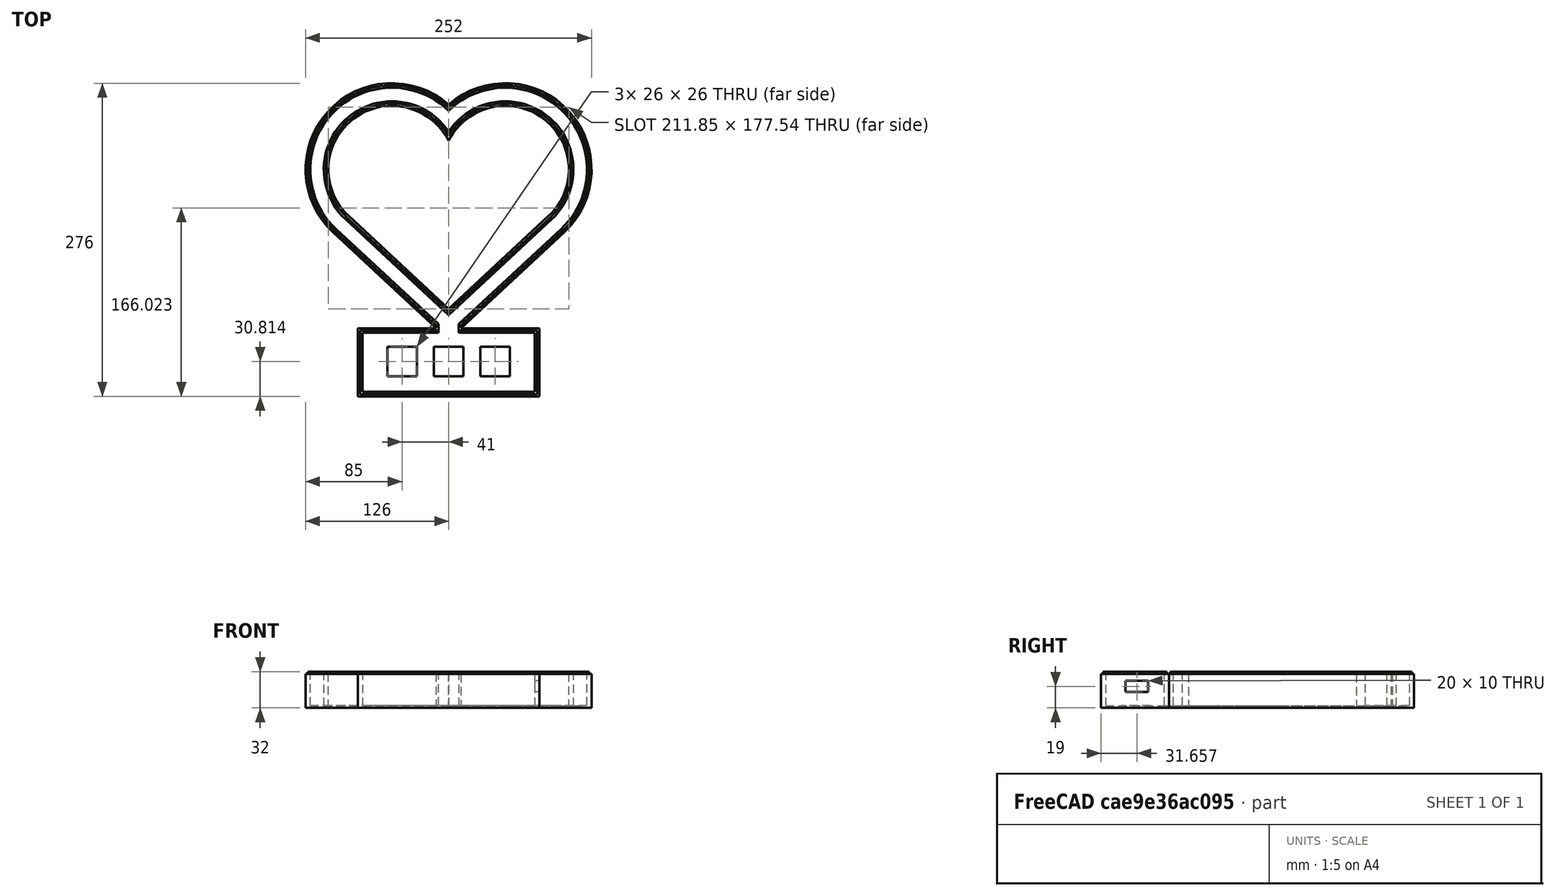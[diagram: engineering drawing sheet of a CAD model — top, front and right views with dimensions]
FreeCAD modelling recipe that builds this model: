
FCSTD DOCUMENT  (FreeCAD 0.19R24291 (Git))
Label: heart_tube_bottom_thick
License: All rights reserved
LicenseURL: http://en.wikipedia.org/wiki/All_rights_reserved
objects: TechDraw::DrawViewDimension×15, Sketcher::SketchObject×12, PartDesign::Pocket×7, PartDesign::Pad×5, TechDraw::DrawViewPart×2, PartDesign::Body×1, TechDraw::DrawSVGTemplate×1, TechDraw::DrawViewDetail×1, TechDraw::DrawPage×1
note: 37 computed .brp shape members not serialized (recipe doc carries the construction recipe); baked Part::Feature solids carry a one-line shape summary decoded from their .brp

FEATURE [Sketcher::SketchObject] Sketch
  AttachmentOffset = pos=(0,0,32) rot=(0,0,1;0rad)
  FullyConstrained = true
  MapMode = 5
  Placement = pos=(0,0,32) rot=(0,0,1;0rad)
  Support = -> [XY_Plane]
  sketch-geometry (4):
    g0: ArcOfCircle CenterX=-50 CenterY=0 CenterZ=0 NormalX=0 NormalY=0 NormalZ=1 AngleXU=0 Radius=56 StartAngle=0.467146 EndAngle=3.96463
    g1: ArcOfCircle CenterX=50 CenterY=0 CenterZ=0 NormalX=0 NormalY=0 NormalZ=1 AngleXU=0 Radius=56 StartAngle=5.46015 EndAngle=8.95763
    g2: LineSegment StartX=-88.08 StartY=-41.0599 StartZ=0 EndX=0 EndY=-122.748 EndZ=0
    g3: LineSegment StartX=0 StartY=-122.748 StartZ=0 EndX=88.08 EndY=-41.0599 EndZ=0
  constraints (11):
    c: Symmetric(g0,g1,g-2)
    c: Equal(g1,g0)
    c: Coincident(g0,g1)
    c: PointOnObject(g2,g-2)
    c: Coincident(g3,g2)
    c: Tangent(g3,g1) = -1.5708
    c: Tangent(g2,g0) = -1.5708
    c: DistanceX(g0,g1) = 100
    c: PointOnObject(g1,g-1)
    c: Distance(g-1,g2) = 90
    c: Radius(g1) = 56
FEATURE [Sketcher::SketchObject] Sketch001
  FullyConstrained = true
  MapMode = 5
  Support = -> [XY_Plane]
  sketch-geometry (4):
    g0: ArcOfCircle CenterX=-50 CenterY=0 CenterZ=0 NormalX=0 NormalY=0 NormalZ=1 AngleXU=0 Radius=76 StartAngle=0.852776 EndAngle=3.96463
    g1: ArcOfCircle CenterX=50 CenterY=0 CenterZ=0 NormalX=0 NormalY=0 NormalZ=1 AngleXU=0 Radius=76 StartAngle=5.46015 EndAngle=8.572
    g2: LineSegment StartX=-101.68 StartY=-55.7241 StartZ=0 EndX=0 EndY=-150.025 EndZ=0
    g3: LineSegment StartX=0 StartY=-150.025 StartZ=0 EndX=101.68 EndY=-55.7241 EndZ=0
  constraints (11):
    c: Symmetric(g0,g1,g-2)
    c: Equal(g1,g0)
    c: Coincident(g0,g1)
    c: PointOnObject(g2,g-2)
    c: Coincident(g3,g2)
    c: Tangent(g3,g1) = -1.5708
    c: Tangent(g2,g0) = -1.5708
    c: DistanceX(g0,g1) = 100
    c: PointOnObject(g1,g-1)
    c: Distance(g-1,g2) = 110
    c: Radius(g1) = 76
FEATURE [Sketcher::SketchObject] Sketch002
  FullyConstrained = true
  MapMode = 5
  Support = -> [XY_Plane]
  sketch-geometry (4):
    g0: ArcOfCircle CenterX=-50 CenterY=0 CenterZ=0 NormalX=0 NormalY=0 NormalZ=1 AngleXU=0 Radius=74 StartAngle=0.828915 EndAngle=3.96463
    g1: ArcOfCircle CenterX=50 CenterY=0 CenterZ=0 NormalX=0 NormalY=0 NormalZ=1 AngleXU=0 Radius=74 StartAngle=5.46015 EndAngle=8.59586
    g2: LineSegment StartX=-100.32 StartY=-54.2577 StartZ=0 EndX=0 EndY=-147.297 EndZ=0
    g3: LineSegment StartX=0 StartY=-147.297 StartZ=0 EndX=100.32 EndY=-54.2577 EndZ=0
  constraints (11):
    c: Symmetric(g0,g1,g-2)
    c: Equal(g1,g0)
    c: Coincident(g0,g1)
    c: PointOnObject(g2,g-2)
    c: Coincident(g3,g2)
    c: Tangent(g3,g1) = -1.5708
    c: Tangent(g2,g0) = -1.5708
    c: DistanceX(g0,g1) = 100
    c: PointOnObject(g1,g-1)
    c: Distance(g-1,g2) = 108
    c: Radius(g1) = 74
FEATURE [Sketcher::SketchObject] Sketch003
  AttachmentOffset = pos=(0,0,32) rot=(0,0,1;0rad)
  FullyConstrained = true
  MapMode = 5
  Placement = pos=(0,0,32) rot=(0,0,1;0rad)
  Support = -> [XY_Plane]
  sketch-geometry (4):
    g0: ArcOfCircle CenterX=-50 CenterY=0 CenterZ=0 NormalX=0 NormalY=0 NormalZ=1 AngleXU=0 Radius=58 StartAngle=0.531458 EndAngle=3.96463
    g1: ArcOfCircle CenterX=50 CenterY=0 CenterZ=0 NormalX=0 NormalY=0 NormalZ=1 AngleXU=0 Radius=58 StartAngle=5.46015 EndAngle=8.89332
    g2: LineSegment StartX=-89.44 StartY=-42.5263 StartZ=0 EndX=0 EndY=-125.475 EndZ=0
    g3: LineSegment StartX=0 StartY=-125.475 StartZ=0 EndX=89.44 EndY=-42.5263 EndZ=0
  constraints (11):
    c: Symmetric(g0,g1,g-2)
    c: Equal(g1,g0)
    c: Coincident(g0,g1)
    c: PointOnObject(g2,g-2)
    c: Coincident(g3,g2)
    c: Tangent(g3,g1) = -1.5708
    c: Tangent(g2,g0) = -1.5708
    c: DistanceX(g0,g1) = 100
    c: PointOnObject(g1,g-1)
    c: Distance(g-1,g2) = 92
    c: Radius(g1) = 58
FEATURE [PartDesign::Pad] Pad
  Direction = (1,1,1)
  Length = 30
  Length2 = 100
  Profile = -> Sketch001
  Refine = true
  Type = 0
FEATURE [Sketcher::SketchObject] Sketch004
  FullyConstrained = true
  MapMode = 5
  Support = -> [XY_Plane]
  sketch-geometry (4):
    g0: LineSegment StartX=-80 StartY=-140 StartZ=0 EndX=80 EndY=-140 EndZ=0
    g1: LineSegment StartX=80 StartY=-140 StartZ=0 EndX=80 EndY=-200 EndZ=0
    g2: LineSegment StartX=80 StartY=-200 StartZ=0 EndX=-80 EndY=-200 EndZ=0
    g3: LineSegment StartX=-80 StartY=-200 StartZ=0 EndX=-80 EndY=-140 EndZ=0
  constraints (11):
    c: Coincident(g0,g1)
    c: Coincident(g1,g2)
    c: Coincident(g2,g3)
    c: Coincident(g3,g0)
    c: Horizontal(g2)
    c: Vertical(g1)
    c: Vertical(g3)
    c: DistanceY(g1,g1) = 60
    c: DistanceX(g0,g0) = 160
    c: Symmetric(g0,g0,g-2)
    c: DistanceY(g0,g-1) = 140
FEATURE [Sketcher::SketchObject] Sketch005
  FullyConstrained = true
  MapMode = 5
  Support = -> [XY_Plane]
  sketch-geometry (4):
    g0: LineSegment StartX=-78 StartY=-142 StartZ=0 EndX=78 EndY=-142 EndZ=0
    g1: LineSegment StartX=78 StartY=-142 StartZ=0 EndX=78 EndY=-198 EndZ=0
    g2: LineSegment StartX=78 StartY=-198 StartZ=0 EndX=-78 EndY=-198 EndZ=0
    g3: LineSegment StartX=-78 StartY=-198 StartZ=0 EndX=-78 EndY=-142 EndZ=0
  constraints (11):
    c: Coincident(g0,g1)
    c: Coincident(g1,g2)
    c: Coincident(g2,g3)
    c: Coincident(g3,g0)
    c: Horizontal(g2)
    c: Vertical(g1)
    c: Vertical(g3)
    c: DistanceY(g1,g1) = 56
    c: DistanceX(g0,g0) = 156
    c: Symmetric(g0,g0,g-2)
    c: DistanceY(g0,g-1) = 142
FEATURE [Sketcher::SketchObject] Sketch006
  AttachmentOffset = pos=(0,0,32) rot=(0,0,1;0rad)
  FullyConstrained = false
  MapMode = 5
  Placement = pos=(0,0,32) rot=(0,0,1;0rad)
  Support = -> [XY_Plane]
  sketch-geometry (4):
    g0: LineSegment StartX=-9 StartY=-136.077 StartZ=0 EndX=9 EndY=-136.077 EndZ=0
    g1: LineSegment StartX=9 StartY=-136.077 StartZ=0 EndX=9 EndY=-148.077 EndZ=0
    g2: LineSegment StartX=9 StartY=-148.077 StartZ=0 EndX=-9 EndY=-148.077 EndZ=0
    g3: LineSegment StartX=-9 StartY=-148.077 StartZ=0 EndX=-9 EndY=-136.077 EndZ=0
  constraints (10):
    c: Coincident(g0,g1)
    c: Coincident(g1,g2)
    c: Coincident(g2,g3)
    c: Coincident(g3,g0)
    c: Horizontal(g0)
    c: Vertical(g1)
    c: Vertical(g3)
    c: DistanceY(g1,g1) = 12
    c: DistanceX(g0,g0) = 18
    c: Symmetric(g1,g2,g-2)
FEATURE [PartDesign::Pad] Pad003
  BaseFeature = -> Pad
  Direction = (1,1,1)
  Length = 32
  Length2 = 100
  Profile = -> Sketch002
  Refine = true
  Type = 0
FEATURE [Sketcher::SketchObject] Sketch007
  AttachmentOffset = pos=(0,0,32) rot=(0,0,1;0rad)
  FullyConstrained = true
  MapMode = 5
  Placement = pos=(0,0,32) rot=(0,0,1;0rad)
  Support = -> [XY_Plane]
  sketch-geometry (4):
    g0: ArcOfCircle CenterX=-50 CenterY=0 CenterZ=0 NormalX=0 NormalY=0 NormalZ=1 AngleXU=0 Radius=72 StartAngle=0.803149 EndAngle=3.96463
    g1: ArcOfCircle CenterX=50 CenterY=0 CenterZ=0 NormalX=0 NormalY=0 NormalZ=1 AngleXU=0 Radius=72 StartAngle=5.46015 EndAngle=8.62163
    g2: LineSegment StartX=-98.96 StartY=-52.7913 StartZ=0 EndX=-1.42e-14 EndY=-144.569 EndZ=0
    g3: LineSegment StartX=-1.42e-14 StartY=-144.569 StartZ=0 EndX=98.96 EndY=-52.7913 EndZ=0
  constraints (11):
    c: Symmetric(g0,g1,g-2)
    c: Equal(g1,g0)
    c: Coincident(g0,g1)
    c: PointOnObject(g2,g-2)
    c: Coincident(g3,g2)
    c: Tangent(g3,g1) = -1.5708
    c: Tangent(g2,g0) = -1.5708
    c: DistanceX(g0,g1) = 100
    c: PointOnObject(g1,g-1)
    c: Distance(g-1,g2) = 106
    c: Radius(g1) = 72
FEATURE [PartDesign::Pocket] Pocket
  BaseFeature = -> Pad003
  Length = 30
  Length2 = 100
  Profile = -> Sketch007
  Refine = true
  Type = 0
FEATURE [Sketcher::SketchObject] Sketch008
  FullyConstrained = true
  MapMode = 5
  Support = -> [XY_Plane]
  sketch-geometry (4):
    g0: ArcOfCircle CenterX=-50 CenterY=0 CenterZ=0 NormalX=0 NormalY=0 NormalZ=1 AngleXU=0 Radius=60 StartAngle=0.585686 EndAngle=3.96463
    g1: ArcOfCircle CenterX=50 CenterY=0 CenterZ=0 NormalX=0 NormalY=0 NormalZ=1 AngleXU=0 Radius=60 StartAngle=5.46015 EndAngle=8.83909
    g2: LineSegment StartX=-90.8 StartY=-43.9927 StartZ=0 EndX=0 EndY=-128.203 EndZ=0
    g3: LineSegment StartX=0 StartY=-128.203 StartZ=0 EndX=90.8 EndY=-43.9927 EndZ=0
  constraints (11):
    c: Symmetric(g0,g1,g-2)
    c: Equal(g1,g0)
    c: Coincident(g0,g1)
    c: PointOnObject(g2,g-2)
    c: Coincident(g3,g2)
    c: Tangent(g3,g1) = -1.5708
    c: Tangent(g2,g0) = -1.5708
    c: DistanceX(g0,g1) = 100
    c: PointOnObject(g1,g-1)
    c: Distance(g-1,g2) = 94
    c: Radius(g1) = 60
FEATURE [PartDesign::Pad] Pad004
  BaseFeature = -> Pocket
  Direction = (1,1,1)
  Length = 32
  Length2 = 100
  Profile = -> Sketch008
  Refine = true
  Type = 0
FEATURE [PartDesign::Pocket] Pocket004
  BaseFeature = -> Pad004
  Length = 2
  Length2 = 100
  Profile = -> Sketch003
  Refine = true
  Type = 0
FEATURE [PartDesign::Pocket] Pocket001
  BaseFeature = -> Pocket004
  Length = 25
  Length2 = 100
  Profile = -> Sketch
  Refine = true
  Type = 1
FEATURE [PartDesign::Pad] Pad002
  BaseFeature = -> Pocket001
  Direction = (1,1,1)
  Length = 30
  Length2 = 100
  Profile = -> Sketch004
  Refine = true
  Type = 0
FEATURE [Sketcher::SketchObject] Sketch009
  AttachmentOffset = pos=(0,0,32) rot=(0,0,1;0rad)
  FullyConstrained = true
  MapMode = 5
  Placement = pos=(0,0,32) rot=(0,0,1;0rad)
  Support = -> [XY_Plane]
  sketch-geometry (4):
    g0: LineSegment StartX=-76 StartY=-144 StartZ=0 EndX=76 EndY=-144 EndZ=0
    g1: LineSegment StartX=76 StartY=-144 StartZ=0 EndX=76 EndY=-196 EndZ=0
    g2: LineSegment StartX=76 StartY=-196 StartZ=0 EndX=-76 EndY=-196 EndZ=0
    g3: LineSegment StartX=-76 StartY=-196 StartZ=0 EndX=-76 EndY=-144 EndZ=0
  constraints (11):
    c: Coincident(g0,g1)
    c: Coincident(g1,g2)
    c: Coincident(g2,g3)
    c: Coincident(g3,g0)
    c: Horizontal(g2)
    c: Vertical(g1)
    c: Vertical(g3)
    c: DistanceY(g1,g1) = 52
    c: DistanceX(g0,g0) = 152
    c: Symmetric(g0,g0,g-2)
    c: DistanceY(g0,g-1) = 144
FEATURE [PartDesign::Pad] Pad005
  BaseFeature = -> Pad002
  Direction = (1,1,1)
  Length = 32
  Length2 = 100
  Profile = -> Sketch005
  Refine = true
  Type = 0
FEATURE [PartDesign::Pocket] Pocket006
  BaseFeature = -> Pad005
  Length = 30
  Length2 = 100
  Profile = -> Sketch009
  Refine = true
  Type = 0
FEATURE [PartDesign::Pocket] Pocket005
  BaseFeature = -> Pocket006
  Length = 30
  Length2 = 100
  Profile = -> Sketch006
  Refine = true
  Type = 0
FEATURE [Sketcher::SketchObject] Sketch010
  AttachmentOffset = pos=(0,0,80) rot=(0,0,1;0rad)
  ExternalGeometry = -> [Pocket005]
  FullyConstrained = false
  MapMode = 5
  Placement = pos=(80,-1.78e-14,1.78e-14) rot=(0.57735,0.57735,0.57735;2.0944rad)
  Support = -> [YZ_Plane]
  sketch-geometry (4):
    g0: LineSegment StartX=-178.343 StartY=24 StartZ=0 EndX=-158.343 EndY=24 EndZ=0
    g1: LineSegment StartX=-158.343 StartY=24 StartZ=0 EndX=-158.343 EndY=14 EndZ=0
    g2: LineSegment StartX=-158.343 StartY=14 StartZ=0 EndX=-178.343 EndY=14 EndZ=0
    g3: LineSegment StartX=-178.343 StartY=14 StartZ=0 EndX=-178.343 EndY=24 EndZ=0
  constraints (11):
    c: Coincident(g0,g1)
    c: Coincident(g1,g2)
    c: Coincident(g2,g3)
    c: Coincident(g3,g0)
    c: Horizontal(g0)
    c: Horizontal(g2)
    c: Vertical(g1)
    c: Vertical(g3)
    c: DistanceX(g0,g0) = 20
    c: DistanceY(g1,g1) = 10
    c: DistanceY(g-3,g1) = 12
FEATURE [PartDesign::Pocket] Pocket007
  BaseFeature = -> Pocket005
  Length = 10
  Length2 = 100
  Midplane = true
  Profile = -> Sketch010
  Refine = true
  Type = 0
FEATURE [Sketcher::SketchObject] Sketch011
  FullyConstrained = false
  MapMode = 5
  Support = -> [XY_Plane]
  sketch-geometry (12):
    g0: LineSegment StartX=-54 StartY=-156.186 StartZ=0 EndX=-28 EndY=-156.186 EndZ=0
    g1: LineSegment StartX=-28 StartY=-156.186 StartZ=0 EndX=-28 EndY=-182.186 EndZ=0
    g2: LineSegment StartX=-28 StartY=-182.186 StartZ=0 EndX=-54 EndY=-182.186 EndZ=0
    g3: LineSegment StartX=-54 StartY=-182.186 StartZ=0 EndX=-54 EndY=-156.186 EndZ=0
    g4: LineSegment StartX=-13 StartY=-156.186 StartZ=0 EndX=13 EndY=-156.186 EndZ=0
    g5: LineSegment StartX=13 StartY=-156.186 StartZ=0 EndX=13 EndY=-182.186 EndZ=0
    g6: LineSegment StartX=13 StartY=-182.186 StartZ=0 EndX=-13 EndY=-182.186 EndZ=0
    g7: LineSegment StartX=-13 StartY=-182.186 StartZ=0 EndX=-13 EndY=-156.186 EndZ=0
    g8: LineSegment StartX=28 StartY=-156.186 StartZ=0 EndX=54 EndY=-156.186 EndZ=0
    g9: LineSegment StartX=54 StartY=-156.186 StartZ=0 EndX=54 EndY=-182.186 EndZ=0
    g10: LineSegment StartX=54 StartY=-182.186 StartZ=0 EndX=28 EndY=-182.186 EndZ=0
    g11: LineSegment StartX=28 StartY=-182.186 StartZ=0 EndX=28 EndY=-156.186 EndZ=0
  constraints (34):
    c: Coincident(g0,g1)
    c: Coincident(g1,g2)
    c: Coincident(g2,g3)
    c: Coincident(g3,g0)
    c: Horizontal(g0)
    c: Horizontal(g2)
    c: Vertical(g1)
    c: Vertical(g3)
    c: DistanceY(g1,g1) = 26
    c: Equal(g0,g3)
    c: Coincident(g4,g5)
    c: Coincident(g5,g6)
    c: Coincident(g6,g7)
    c: Coincident(g7,g4)
    c: Horizontal(g6)
    c: Vertical(g5)
    c: Vertical(g7)
    c: Coincident(g8,g9)
    c: Coincident(g9,g10)
    c: Coincident(g10,g11)
    c: Coincident(g11,g8)
    c: Horizontal(g8)
    c: Horizontal(g10)
    c: Vertical(g9)
    c: Vertical(g11)
    c: Equal(g1,g4)
    c: Equal(g5,g4)
    c: Equal(g4,g8)
    c: Equal(g8,g9)
    c: Horizontal(g8,g4)
    c: Horizontal(g4,g0)
    c: DistanceX(g0,g4) = 15
    c: DistanceX(g4,g8) = 15
    c: Symmetric(g4,g4,g-2)
FEATURE [PartDesign::Pocket] Pocket008
  BaseFeature = -> Pocket007
  Length = 5
  Length2 = 100
  Midplane = true
  Profile = -> Sketch011
  Refine = true
  Type = 0
FEATURE [PartDesign::Body] Body
  Group = -> [Sketch001,Sketch002,Sketch,Pad,Pad003,Pocket,Pad004,Pocket004,Pocket001,Sketch003,Sketch004,Pad002,Sketch005,Sketch006,Sketch007,Sketch008,Sketch009,Pad005,Pocket006,Pocket005,Sketch010,Pocket007,Sketch011,Pocket008]
  Origin = -> Origin
  Tip = -> Pocket008
FEATURE [TechDraw::DrawSVGTemplate] Template
  Height = 297
  Orientation = 1
  Width = 420
FEATURE [TechDraw::DrawViewPart] View
  CoarseView = false
  Direction = (0,0,1)
  Focus = 100
  HardHidden = false
  IsoCount = 0
  IsoHidden = false
  IsoVisible = false
  LockPosition = false
  Perspective = false
  Rotation = 0
  Scale = 0.5
  ScaleType = 0
  SeamHidden = false
  SeamVisible = true
  SmoothHidden = false
  SmoothVisible = true
  Source = -> [Pocket008]
  X = 111.445
  XDirection = (1,0,0)
  Y = 188.919
FEATURE [TechDraw::DrawViewPart] View001
  CoarseView = false
  Direction = (0.577,-0.577,0.577)
  Focus = 100
  HardHidden = false
  IsoCount = 0
  IsoHidden = false
  IsoVisible = false
  LockPosition = false
  Perspective = false
  Rotation = 0
  Scale = 0.5
  ScaleType = 0
  SeamHidden = false
  SeamVisible = true
  SmoothHidden = false
  SmoothVisible = true
  Source = -> [Pocket008]
  X = 281.398
  XDirection = (0.707,0.707,0)
  Y = 208.914
FEATURE [TechDraw::DrawViewDimension] Dimension
  Arbitrary = false
  ArbitraryTolerances = false
  EqualTolerance = true
  FormatSpec = %.2f
  FormatSpecOverTolerance = %+.2f
  FormatSpecUnderTolerance = %+.2f
  Inverted = false
  LockPosition = false
  MeasureType = 1
  OverTolerance = 0
  References2D = -> [View]
  Rotation = 0
  ScaleType = 0
  TheoreticalExact = false
  Type = 1
  UnderTolerance = 0
  X = 44.3105
  Y = -28.4641
FEATURE [TechDraw::DrawViewDimension] Dimension001
  Arbitrary = false
  ArbitraryTolerances = false
  EqualTolerance = true
  FormatSpec = %.2f
  FormatSpecOverTolerance = %+.2f
  FormatSpecUnderTolerance = %+.2f
  Inverted = false
  LockPosition = false
  MeasureType = 1
  OverTolerance = 0
  References2D = -> [View]
  Rotation = 0
  ScaleType = 0
  TheoreticalExact = false
  Type = 1
  UnderTolerance = 0
  X = 47.9796
  Y = -37.5288
FEATURE [TechDraw::DrawViewDimension] Dimension002
  Arbitrary = false
  ArbitraryTolerances = false
  EqualTolerance = true
  FormatSpec = %.2f
  FormatSpecOverTolerance = %+.2f
  FormatSpecUnderTolerance = %+.2f
  Inverted = false
  LockPosition = false
  MeasureType = 1
  OverTolerance = 0
  References2D = -> [View]
  Rotation = 0
  ScaleType = 0
  TheoreticalExact = false
  Type = 1
  UnderTolerance = 0
  X = 52.1929
  Y = -56.8388
FEATURE [TechDraw::DrawViewDimension] Dimension003
  Arbitrary = false
  ArbitraryTolerances = false
  EqualTolerance = true
  FormatSpec = %.2f
  FormatSpecOverTolerance = %+.2f
  FormatSpecUnderTolerance = %+.2f
  Inverted = false
  LockPosition = false
  MeasureType = 1
  OverTolerance = 0
  References2D = -> [View]
  Rotation = 0
  ScaleType = 0
  TheoreticalExact = false
  Type = 1
  UnderTolerance = 0
  X = 48.4512
  Y = -47.6589
FEATURE [TechDraw::DrawViewDimension] Dimension004
  Arbitrary = false
  ArbitraryTolerances = false
  EqualTolerance = true
  FormatSpec = %.2f
  FormatSpecOverTolerance = %+.2f
  FormatSpecUnderTolerance = %+.2f
  Inverted = false
  LockPosition = false
  MeasureType = 1
  OverTolerance = 0
  References2D = -> [View]
  Rotation = 0
  ScaleType = 0
  TheoreticalExact = false
  Type = 1
  UnderTolerance = 0
  X = 1.86762
  Y = -70.0187
FEATURE [TechDraw::DrawViewDimension] Dimension005
  Arbitrary = false
  ArbitraryTolerances = false
  EqualTolerance = true
  FormatSpec = %.2f
  FormatSpecOverTolerance = %+.2f
  FormatSpecUnderTolerance = %+.2f
  Inverted = false
  LockPosition = false
  MeasureType = 1
  OverTolerance = 0
  References2D = -> [View]
  Rotation = 0
  ScaleType = 0
  TheoreticalExact = false
  Type = 2
  UnderTolerance = 0
  X = -45.7726
  Y = -54.1698
FEATURE [TechDraw::DrawViewDimension] Dimension006
  Arbitrary = false
  ArbitraryTolerances = false
  EqualTolerance = true
  FormatSpec = R%.2f
  FormatSpecOverTolerance = %+.2f
  FormatSpecUnderTolerance = %+.2f
  Inverted = false
  LockPosition = false
  MeasureType = 1
  OverTolerance = 0
  References2D = -> [View]
  Rotation = 0
  ScaleType = 0
  TheoreticalExact = false
  Type = 4
  UnderTolerance = 0
  X = -14.0125
  Y = 47.951
FEATURE [TechDraw::DrawViewDimension] Dimension007
  Arbitrary = false
  ArbitraryTolerances = false
  EqualTolerance = true
  FormatSpec = R%.2f
  FormatSpecOverTolerance = %+.2f
  FormatSpecUnderTolerance = %+.2f
  Inverted = false
  LockPosition = false
  MeasureType = 1
  OverTolerance = 0
  References2D = -> [View]
  Rotation = 0
  ScaleType = 0
  TheoreticalExact = false
  Type = 4
  UnderTolerance = 0
  X = -24.1041
  Y = 46.0656
FEATURE [TechDraw::DrawViewDimension] Dimension008
  Arbitrary = false
  ArbitraryTolerances = false
  EqualTolerance = true
  FormatSpec = R%.2f
  FormatSpecOverTolerance = %+.2f
  FormatSpecUnderTolerance = %+.2f
  Inverted = false
  LockPosition = false
  MeasureType = 1
  OverTolerance = 0
  References2D = -> [View]
  Rotation = 0
  ScaleType = 0
  TheoreticalExact = false
  Type = 4
  UnderTolerance = 0
  X = -36.4239
  Y = 43.6552
FEATURE [TechDraw::DrawViewDimension] Dimension009
  Arbitrary = false
  ArbitraryTolerances = false
  EqualTolerance = true
  FormatSpec = R%.2f
  FormatSpecOverTolerance = %+.2f
  FormatSpecUnderTolerance = %+.2f
  Inverted = false
  LockPosition = false
  MeasureType = 1
  OverTolerance = 0
  References2D = -> [View]
  Rotation = 0
  ScaleType = 0
  TheoreticalExact = false
  Type = 4
  UnderTolerance = 0
  X = -70.9731
  Y = 49.2794
FEATURE [TechDraw::DrawViewDimension] Dimension010
  Arbitrary = false
  ArbitraryTolerances = false
  EqualTolerance = true
  FormatSpec = R%.2f
  FormatSpecOverTolerance = %+.2f
  FormatSpecUnderTolerance = %+.2f
  Inverted = false
  LockPosition = false
  MeasureType = 1
  OverTolerance = 0
  References2D = -> [View]
  Rotation = 0
  ScaleType = 0
  TheoreticalExact = false
  Type = 4
  UnderTolerance = 0
  X = -79.0078
  Y = 40.9769
FEATURE [TechDraw::DrawViewDimension] Dimension011
  Arbitrary = false
  ArbitraryTolerances = false
  EqualTolerance = true
  FormatSpec = R%.2f
  FormatSpecOverTolerance = %+.2f
  FormatSpecUnderTolerance = %+.2f
  Inverted = false
  LockPosition = false
  MeasureType = 1
  OverTolerance = 0
  References2D = -> [View]
  Rotation = 0
  ScaleType = 0
  TheoreticalExact = false
  Type = 4
  UnderTolerance = 0
  X = -81.9539
  Y = 30.7997
FEATURE [TechDraw::DrawViewDetail] Detail
  AnchorPoint = (78,-80,0)
  BaseView = -> View
  CoarseView = false
  Direction = (0,0,1)
  Focus = 100
  HardHidden = false
  IsoCount = 0
  IsoHidden = false
  IsoVisible = false
  LockPosition = false
  Perspective = false
  Radius = 6
  Reference = 1
  Rotation = 0
  Scale = 4.5
  ScaleType = 2
  SeamHidden = false
  SeamVisible = true
  SmoothHidden = false
  SmoothVisible = true
  Source = -> [Pocket008]
  X = 85.1412
  XDirection = (1,0,0)
  Y = 64.6893
FEATURE [TechDraw::DrawViewDimension] Dimension012
  Arbitrary = false
  ArbitraryTolerances = false
  EqualTolerance = true
  FormatSpec = %.2f
  FormatSpecOverTolerance = %+.2f
  FormatSpecUnderTolerance = %+.2f
  Inverted = false
  LockPosition = false
  MeasureType = 1
  OverTolerance = 0
  References2D = -> [Detail]
  Rotation = 0
  ScaleType = 0
  TheoreticalExact = false
  Type = 2
  UnderTolerance = 0
  X = -25.1576
  Y = 25.2717
FEATURE [TechDraw::DrawViewDimension] Dimension013
  Arbitrary = false
  ArbitraryTolerances = false
  EqualTolerance = true
  FormatSpec = %.2f
  FormatSpecOverTolerance = %+.2f
  FormatSpecUnderTolerance = %+.2f
  Inverted = false
  LockPosition = false
  MeasureType = 1
  OverTolerance = 0
  References2D = -> [Detail]
  Rotation = 0
  ScaleType = 0
  TheoreticalExact = false
  Type = 2
  UnderTolerance = 0
  X = -16.7081
  Y = 25.7774
FEATURE [TechDraw::DrawViewDimension] Dimension014
  Arbitrary = false
  ArbitraryTolerances = false
  EqualTolerance = true
  FormatSpec = %.2f
  FormatSpecOverTolerance = %+.2f
  FormatSpecUnderTolerance = %+.2f
  Inverted = false
  LockPosition = false
  MeasureType = 1
  OverTolerance = 0
  References2D = -> [View]
  Rotation = 0
  ScaleType = 0
  TheoreticalExact = false
  Type = 0
  UnderTolerance = 0
  X = -15.7565
  Y = -2.5856
FEATURE [TechDraw::DrawPage] Page
  KeepUpdated = true
  NextBalloonIndex = 1
  ProjectionType = 0
  Template = -> Template
  Views = -> [View,View001,Dimension,Dimension001,Dimension002,Dimension003,Dimension004,Dimension005,Dimension006,Dimension007,Dimension008,Dimension009,Dimension010,Dimension011,Detail,Dimension012,Dimension013,Dimension014]
